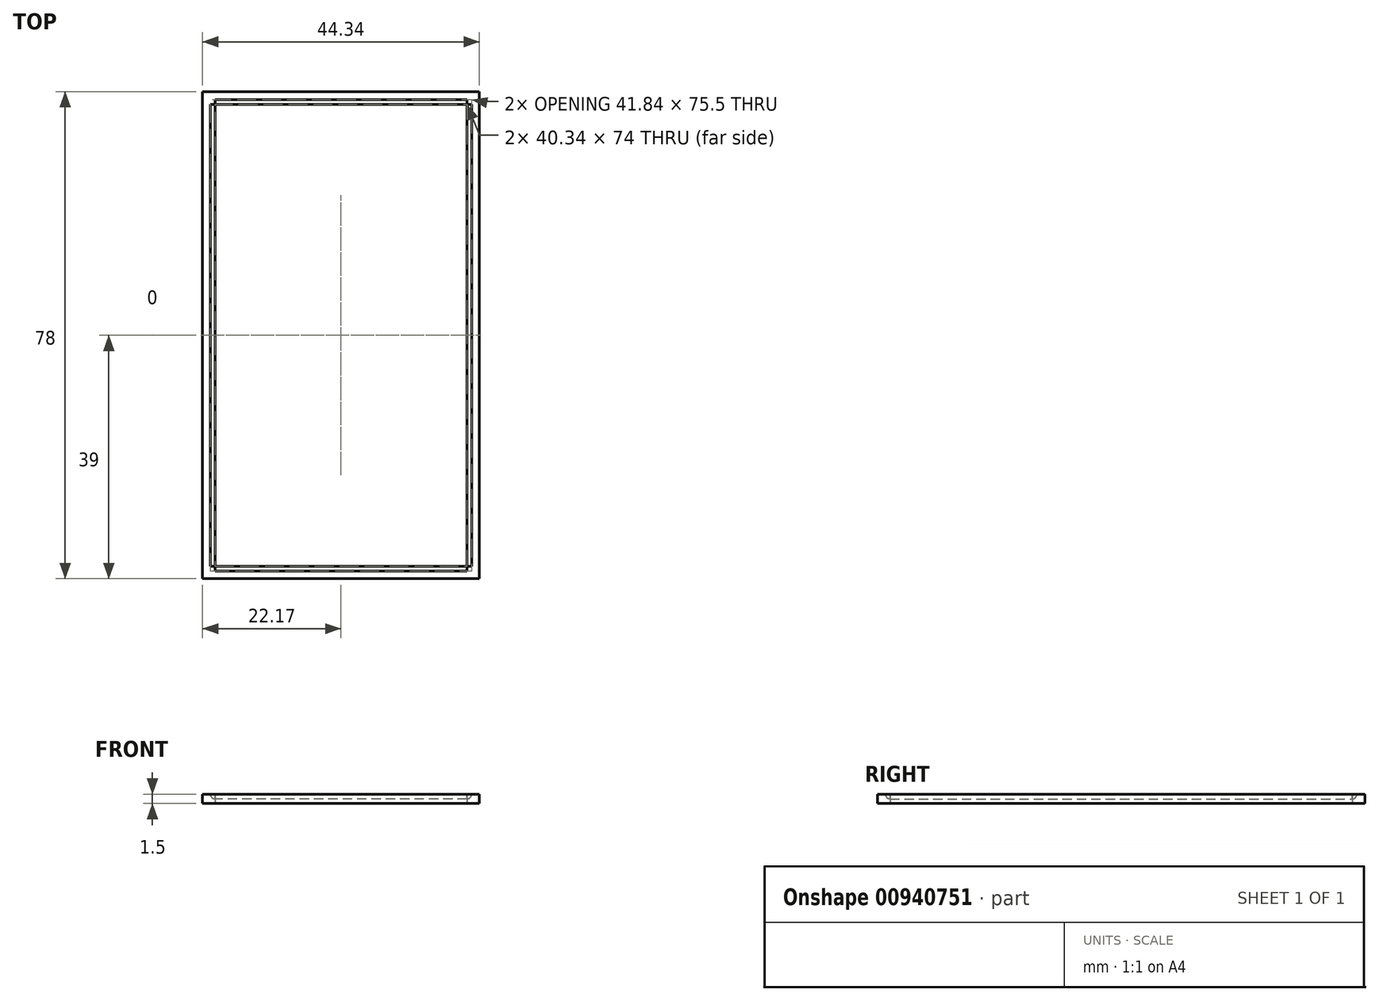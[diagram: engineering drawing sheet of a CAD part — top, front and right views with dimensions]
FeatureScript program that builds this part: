
annotation { "Feature Type Name" : "Feature", "Feature Type Description" : "" }
export const myFeature = defineFeature(function(context is Context, id is Id, definition is map)
    precondition{}
    {
        {
            var Q0;
            Q0=qCreatedBy(makeId("Top.planeOp"),FACE);
            var sketch = newSketch(context, id + "F0", { "sketchPlane" : qUnion([Q0])});
            skLineSegment(sketch, "E0.bottom", {"start": v(0, 0) * mm, "end": v(-44.34, 0) * mm});
            skLineSegment(sketch, "E0.top", {"start": v(0, 78) * mm, "end": v(-44.34, 78) * mm});
            skLineSegment(sketch, "E0.left", {"start": v(0, 0) * mm, "end": v(0, 78) * mm});
            skLineSegment(sketch, "E0.right", {"start": v(-44.34, 0) * mm, "end": v(-44.34, 78) * mm});
            skLineSegment(sketch, "E1.bottom", {"start": v(-42.34, 76) * mm, "end": v(-2, 76) * mm});
            skLineSegment(sketch, "E1.top", {"start": v(-42.34, 2) * mm, "end": v(-2, 2) * mm});
            skLineSegment(sketch, "E1.left", {"start": v(-42.34, 76) * mm, "end": v(-42.34, 2) * mm});
            skLineSegment(sketch, "E1.right", {"start": v(-2, 76) * mm, "end": v(-2, 2) * mm});
            skLineSegment(sketch, "E2", {"start": v(-24.95, 78) * mm, "end": v(-24.95, 76) * mm});
            skLineSegment(sketch, "E3", {"start": v(-42.34, 15.82) * mm, "end": v(-44.34, 15.82) * mm});
            skSolve(sketch);
        }
        {
            var Q0;
            {var subQ4=sQuery(id+"F0.wireOp",EDGE,"E2");Q0=makeQuery(id+"F0.imprint","IMPRINT",FACE,{"disambiguationData":[TD([[makeQuery(id+"F0.imprint","IMPRINT",EDGE,{"derivedFrom":subQ4}),-1.0]])]});}
            var Q1;
            {var subQ1=sQuery(id+"F0.wireOp",EDGE,"E0.bottom");Q1=makeQuery(id+"F0.imprint","IMPRINT",FACE,{"disambiguationData":[TD([[makeQuery(id+"F0.imprint","IMPRINT",EDGE,{"derivedFrom":subQ1}),-1.0]])]});}
            extrude(context, id + "F1", {"entities" : qUnion([Q0, Q1]), "depth" : 1.5 * mm, "offsetDistance" : 25 * mm});
        }
        {
            var Q0;
            Q0=makeQuery(id+"F1.opExtrude","SWEPT_FACE",FACE,{"disambiguationData":[OSD([sQuery(id+"F0.wireOp",EDGE,"E1.left")])]});
            var sketch = newSketch(context, id + "F2", { "sketchPlane" : qUnion([Q0])});
            skCircle(sketch, "E4", {"center": v(76, 1.5) * mm, "radius": 0.75 * mm});
            skCircle(sketch, "E5", {"center": v(2, 1.5) * mm, "radius": 0.75 * mm});
            skSolve(sketch);
        }
        {
            var Q0;
            Q0=makeQuery(id+"F1.opExtrude","SWEPT_FACE",FACE,{"disambiguationData":[OSD([sQuery(id+"F0.wireOp",EDGE,"E1.bottom")])]});
            var sketch = newSketch(context, id + "F3", { "sketchPlane" : qUnion([Q0])});
            skCircle(sketch, "E6", {"center": v(-42.34, 1.5) * mm, "radius": 0.75 * mm});
            skCircle(sketch, "E7", {"center": v(-2, 1.5) * mm, "radius": 0.75 * mm});
            skSolve(sketch);
        }
        {
            var Q0;
            {var subQ0=sQuery(id+"F2.wireOp",EDGE,"E4");var subQ1=sQuery(id+"F0.wireOp",EDGE,"E1.left");var subQ4=makeQuery(id+"F1.opExtrude","CAP_EDGE",EDGE,{"disambiguationData":[OSD([subQ1])],"isStart":false});var subQ5=makeQuery(id+"F2.imprint","INTERSECT",VERTEX,{"derivedFrom":[subQ4,subQ0]});Q0=makeQuery(id+"F2.imprint","IMPRINT",FACE,{"disambiguationData":[TD([[makeQuery(id+"F2.imprint","IMPRINT",EDGE,{"disambiguationData":[TD([[subQ5,1.0]])],"derivedFrom":subQ0}),1.0]])]});}
            var Q1;
            {var subQ0=sQuery(id+"F2.wireOp",EDGE,"E4");var subQ1=sQuery(id+"F0.wireOp",EDGE,"E1.left");var subQ4=makeQuery(id+"F1.opExtrude","CAP_EDGE",EDGE,{"disambiguationData":[OSD([subQ1])],"isStart":false});var subQ5=makeQuery(id+"F2.imprint","INTERSECT",VERTEX,{"derivedFrom":[subQ4,subQ0]});Q1=makeQuery(id+"F2.imprint","IMPRINT",FACE,{"disambiguationData":[TD([[makeQuery(id+"F2.imprint","IMPRINT",EDGE,{"disambiguationData":[TD([[subQ5,-1.0]])],"derivedFrom":subQ0}),1.0]])]});}
            var Q2;
            {var subQ0=sQuery(id+"F2.wireOp",EDGE,"E5");var subQ1=sQuery(id+"F0.wireOp",EDGE,"E1.left");var subQ4=makeQuery(id+"F1.opExtrude","CAP_EDGE",EDGE,{"disambiguationData":[OSD([subQ1])],"isStart":false});var subQ5=makeQuery(id+"F2.imprint","INTERSECT",VERTEX,{"derivedFrom":[subQ4,subQ0]});Q2=makeQuery(id+"F2.imprint","IMPRINT",FACE,{"disambiguationData":[TD([[makeQuery(id+"F2.imprint","IMPRINT",EDGE,{"disambiguationData":[TD([[subQ5,-1.0]])],"derivedFrom":subQ0}),1.0]])]});}
            var Q3;
            {var subQ0=sQuery(id+"F2.wireOp",EDGE,"E5");var subQ1=sQuery(id+"F0.wireOp",EDGE,"E1.left");var subQ4=makeQuery(id+"F1.opExtrude","CAP_EDGE",EDGE,{"disambiguationData":[OSD([subQ1])],"isStart":false});var subQ5=makeQuery(id+"F2.imprint","INTERSECT",VERTEX,{"derivedFrom":[subQ4,subQ0]});Q3=makeQuery(id+"F2.imprint","IMPRINT",FACE,{"disambiguationData":[TD([[makeQuery(id+"F2.imprint","IMPRINT",EDGE,{"disambiguationData":[TD([[subQ5,1.0]])],"derivedFrom":subQ0}),1.0]])]});}
            extrude(context, id + "F4", {"entities" : qUnion([Q0, Q1, Q2, Q3]), "operationType" : NewBodyOperationType.REMOVE, "depth" : 40.34 * mm, "offsetDistance" : 25 * mm});
        }
        {
            var Q0;
            {var subQ0=sQuery(id+"F3.wireOp",EDGE,"E6");var subQ1=sQuery(id+"F0.wireOp",EDGE,"E1.bottom");var subQ4=makeQuery(id+"F1.opExtrude","CAP_EDGE",EDGE,{"disambiguationData":[OSD([subQ1])],"isStart":false});var subQ5=makeQuery(id+"F3.imprint","INTERSECT",VERTEX,{"derivedFrom":[subQ4,subQ0]});Q0=makeQuery(id+"F3.imprint","IMPRINT",FACE,{"disambiguationData":[TD([[makeQuery(id+"F3.imprint","IMPRINT",EDGE,{"disambiguationData":[TD([[subQ5,-1.0]])],"derivedFrom":subQ0}),1.0]])]});}
            var Q1;
            {var subQ0=sQuery(id+"F3.wireOp",EDGE,"E6");var subQ1=sQuery(id+"F0.wireOp",EDGE,"E1.bottom");var subQ4=makeQuery(id+"F1.opExtrude","CAP_EDGE",EDGE,{"disambiguationData":[OSD([subQ1])],"isStart":false});var subQ5=makeQuery(id+"F3.imprint","INTERSECT",VERTEX,{"derivedFrom":[subQ4,subQ0]});Q1=makeQuery(id+"F3.imprint","IMPRINT",FACE,{"disambiguationData":[TD([[makeQuery(id+"F3.imprint","IMPRINT",EDGE,{"disambiguationData":[TD([[subQ5,1.0]])],"derivedFrom":subQ0}),1.0]])]});}
            var Q2;
            {var subQ0=sQuery(id+"F3.wireOp",EDGE,"E7");var subQ1=sQuery(id+"F0.wireOp",EDGE,"E1.bottom");var subQ4=makeQuery(id+"F1.opExtrude","CAP_EDGE",EDGE,{"disambiguationData":[OSD([subQ1])],"isStart":false});var subQ5=makeQuery(id+"F3.imprint","INTERSECT",VERTEX,{"derivedFrom":[subQ4,subQ0]});Q2=makeQuery(id+"F3.imprint","IMPRINT",FACE,{"disambiguationData":[TD([[makeQuery(id+"F3.imprint","IMPRINT",EDGE,{"disambiguationData":[TD([[subQ5,1.0]])],"derivedFrom":subQ0}),1.0]])]});}
            var Q3;
            {var subQ0=sQuery(id+"F3.wireOp",EDGE,"E7");var subQ1=sQuery(id+"F0.wireOp",EDGE,"E1.bottom");var subQ4=makeQuery(id+"F1.opExtrude","CAP_EDGE",EDGE,{"disambiguationData":[OSD([subQ1])],"isStart":false});var subQ5=makeQuery(id+"F3.imprint","INTERSECT",VERTEX,{"derivedFrom":[subQ4,subQ0]});Q3=makeQuery(id+"F3.imprint","IMPRINT",FACE,{"disambiguationData":[TD([[makeQuery(id+"F3.imprint","IMPRINT",EDGE,{"disambiguationData":[TD([[subQ5,-1.0]])],"derivedFrom":subQ0}),1.0]])]});}
            extrude(context, id + "F5", {"entities" : qUnion([Q0, Q1, Q2, Q3]), "operationType" : NewBodyOperationType.REMOVE, "depth" : 74 * mm, "offsetDistance" : 25 * mm});
        }
    });
